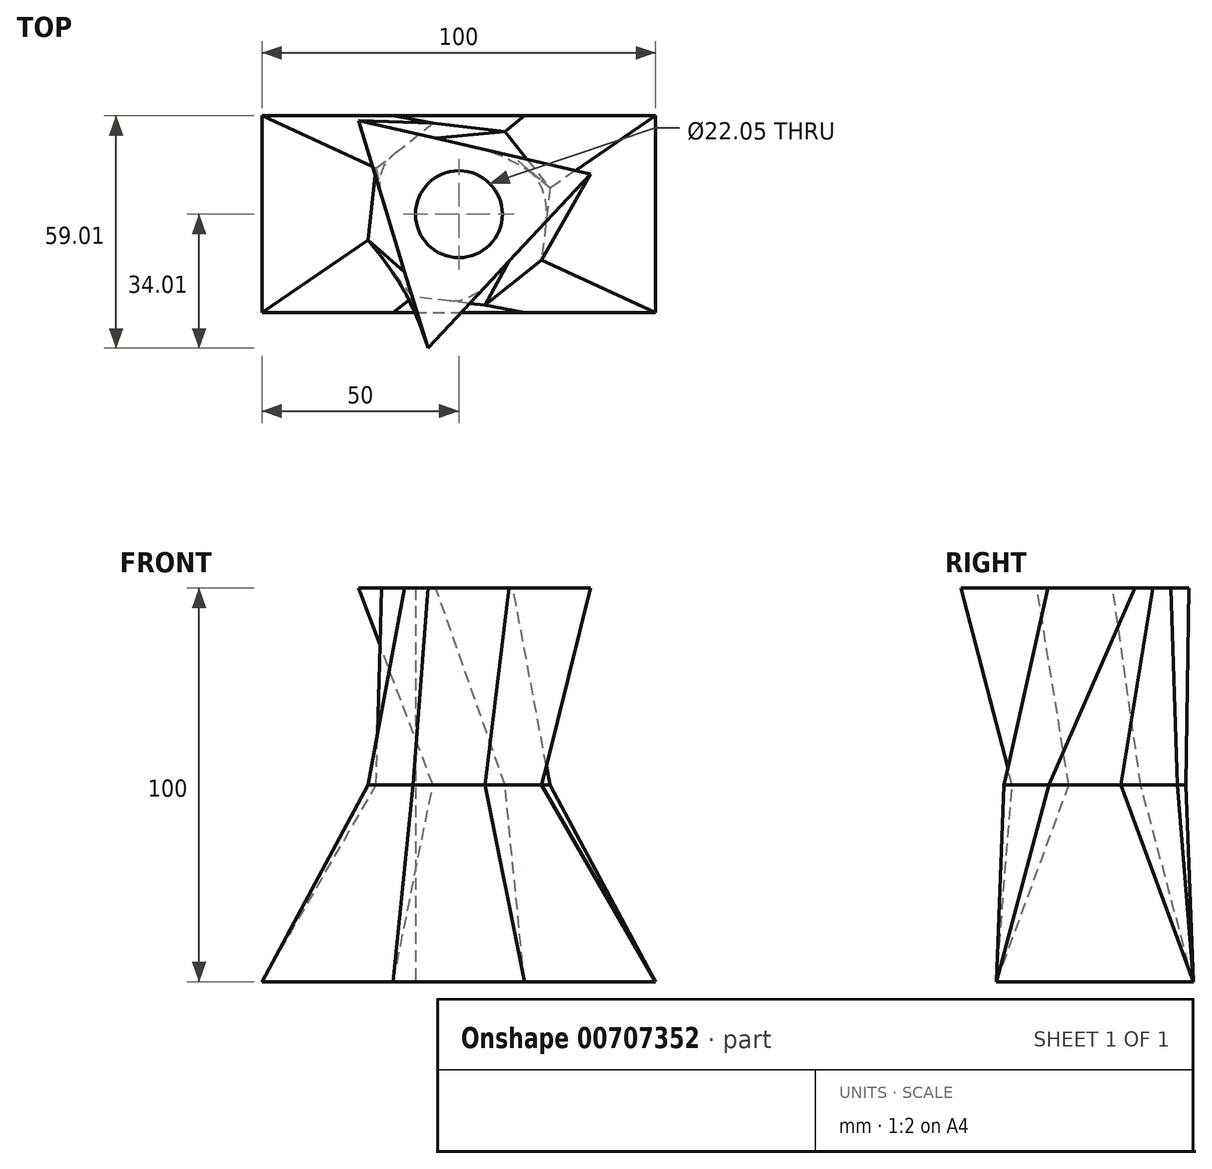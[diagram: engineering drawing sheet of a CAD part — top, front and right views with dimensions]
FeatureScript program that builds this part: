
annotation { "Feature Type Name" : "Feature", "Feature Type Description" : "" }
export const myFeature = defineFeature(function(context is Context, id is Id, definition is map)
    precondition{}
    {
        {
            var Q0;
            Q0=qCreatedBy(makeId("Top.planeOp"),FACE);
            var sketch = newSketch(context, id + "F0", { "sketchPlane" : qUnion([Q0])});
            skLineSegment(sketch, "E0.bottom", {"start": v(-50, 25) * mm, "end": v(50, 25) * mm});
            skLineSegment(sketch, "E0.top", {"start": v(-50, -25) * mm, "end": v(50, -25) * mm});
            skLineSegment(sketch, "E0.left", {"start": v(-50, 25) * mm, "end": v(-50, -25) * mm});
            skLineSegment(sketch, "E0.right", {"start": v(50, 25) * mm, "end": v(50, -25) * mm});
            skSolve(sketch);
        }
        {
            var Q0;
            Q0=makeQuery(id+"F0.imprint","IMPRINT",FACE,{"disambiguationData":[TD([[makeQuery(id+"F0.imprint","IMPRINT",EDGE,{"derivedFrom":sQuery(id+"F0.wireOp",EDGE,"E0.bottom")}),-1.0]])]});
            cPlane(context, id + "F1", {"entities" : qUnion([Q0]), "cplaneType" : CPlaneType.OFFSET, "offset" : 50 * mm, "width" : 150 * mm, "height" : 150 * mm});
        }
        {
            var Q0;
            Q0=makeQuery(id+"F0.imprint","IMPRINT",FACE,{"disambiguationData":[TD([[makeQuery(id+"F0.imprint","IMPRINT",EDGE,{"derivedFrom":sQuery(id+"F0.wireOp",EDGE,"E0.bottom")}),-1.0]])]});
            cPlane(context, id + "F2", {"entities" : qUnion([Q0]), "cplaneType" : CPlaneType.OFFSET, "offset" : 100 * mm, "width" : 150 * mm, "height" : 150 * mm});
        }
        {
            var Q0;
            Q0=qCreatedBy(id+"F2.planeOp",FACE);
            var sketch = newSketch(context, id + "F3", { "sketchPlane" : qUnion([Q0])});
            skCircle(sketch, "E1.cCircle", {"center": v(0, 0) * mm, "radius": 17.45 * mm, "construction": true});
            skLineSegment(sketch, "E1.0", {"start": v(-25.52, 23.82) * mm, "end": v(33.39, 10.19) * mm});
            skLineSegment(sketch, "E1.1", {"start": v(33.39, 10.19) * mm, "end": v(-7.87, -34.01) * mm});
            skLineSegment(sketch, "E1.2", {"start": v(-7.87, -34.01) * mm, "end": v(-25.52, 23.82) * mm});
            skPoint(sketch, "E1.0.midPoint", {"position": v(3.94, 17) * mm});
            skSolve(sketch);
        }
        {
            var Q0;
            Q0=qCreatedBy(id+"F1.planeOp",FACE);
            var sketch = newSketch(context, id + "F4", { "sketchPlane" : qUnion([Q0])});
            skCircle(sketch, "E2.cCircle", {"center": v(0, 0) * mm, "radius": 22.2 * mm, "construction": true});
            skLineSegment(sketch, "E2.0", {"start": v(-6.6, 23.11) * mm, "end": v(11.67, 21.02) * mm});
            skLineSegment(sketch, "E2.1", {"start": v(11.67, 21.02) * mm, "end": v(23.11, 6.6) * mm});
            skLineSegment(sketch, "E2.2", {"start": v(23.11, 6.6) * mm, "end": v(21.02, -11.67) * mm});
            skLineSegment(sketch, "E2.3", {"start": v(21.02, -11.67) * mm, "end": v(6.6, -23.11) * mm});
            skLineSegment(sketch, "E2.4", {"start": v(6.6, -23.11) * mm, "end": v(-11.67, -21.02) * mm});
            skLineSegment(sketch, "E2.5", {"start": v(-11.67, -21.02) * mm, "end": v(-23.11, -6.6) * mm});
            skLineSegment(sketch, "E2.6", {"start": v(-23.11, -6.6) * mm, "end": v(-21.02, 11.67) * mm});
            skLineSegment(sketch, "E2.7", {"start": v(-21.02, 11.67) * mm, "end": v(-6.6, 23.11) * mm});
            skPoint(sketch, "E2.0.midPoint", {"position": v(2.53, 22.06) * mm});
            skSolve(sketch);
        }
        {
            var Q0;
            Q0=makeQuery(id+"F0.imprint","IMPRINT",FACE,{"disambiguationData":[TD([[makeQuery(id+"F0.imprint","IMPRINT",EDGE,{"derivedFrom":sQuery(id+"F0.wireOp",EDGE,"E0.bottom")}),-1.0]])]});
            var Q1;
            Q1=makeQuery(id+"F4.imprint","IMPRINT",FACE,{"disambiguationData":[TD([[makeQuery(id+"F4.imprint","IMPRINT",EDGE,{"derivedFrom":sQuery(id+"F4.wireOp",EDGE,"E2.0")}),-1.0]])]});
            loft(context, id + "F5", {"sheetProfilesArray" : [{ "sheetProfileEntities" : qUnion([Q0]) }, { "sheetProfileEntities" : qUnion([Q1]) }]});
        }
        {
            var Q1;
            Q1=makeQuery(id+"F5.opLoft","CAP_FACE",FACE,{"disambiguationData":[OSD([makeQuery(id+"F4.imprint","IMPRINT",FACE,{"disambiguationData":[TD([[makeQuery(id+"F4.imprint","IMPRINT",EDGE,{"derivedFrom":sQuery(id+"F4.wireOp",EDGE,"E2.0")}),-1.0]])]})])],"isStart":true});
            var Q2;
            Q2=makeQuery(id+"F3.imprint","IMPRINT",FACE,{"disambiguationData":[TD([[makeQuery(id+"F3.imprint","IMPRINT",EDGE,{"derivedFrom":sQuery(id+"F3.wireOp",EDGE,"E1.0")}),-1.0]])]});
            loft(context, id + "F6", {"operationType" : NewBodyOperationType.ADD, "sheetProfilesArray" : [{ "sheetProfileEntities" : qUnion([Q1]) }, { "sheetProfileEntities" : qUnion([Q2]) }]});
        }
        {
            var Q0;
            Q0=makeQuery(id+"F5.opLoft","CAP_FACE",FACE,{"disambiguationData":[OSD([makeQuery(id+"F0.imprint","IMPRINT",FACE,{"disambiguationData":[TD([[makeQuery(id+"F0.imprint","IMPRINT",EDGE,{"derivedFrom":sQuery(id+"F0.wireOp",EDGE,"E0.bottom")}),-1.0]])]})])],"isStart":true});
            var sketch = newSketch(context, id + "F7", { "sketchPlane" : qUnion([Q0])});
            skCircle(sketch, "E3", {"center": v(0, 0) * mm, "radius": 11.02 * mm});
            skSolve(sketch);
        }
        {
            var Q0;
            Q0=makeQuery(id+"F7.imprint","IMPRINT",FACE,{"disambiguationData":[TD([[makeQuery(id+"F7.imprint","IMPRINT",EDGE,{"derivedFrom":sQuery(id+"F7.wireOp",EDGE,"E3")}),1.0]])]});
            extrude(context, id + "F8", {"entities" : qUnion([Q0]), "operationType" : NewBodyOperationType.REMOVE, "endBound" : BoundingType.UP_TO_NEXT, "oppositeDirection" : true, "depth" : 25 * mm, "offsetDistance" : 25 * mm});
        }
    });
